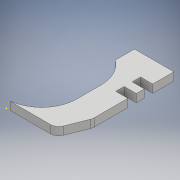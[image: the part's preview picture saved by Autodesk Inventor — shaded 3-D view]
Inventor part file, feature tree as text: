
AUTODESK INVENTOR PART (.ipt)
format: ipt  version: 2017 (Build 210142000, 142)  size: 152,064 bytes
history: native  units: mm
features: sketch x4, extrude x2, hole x1
ambient origin geometry x8: Origin, YZ Plane, XZ Plane, XY Plane, X Axis, Y Axis, Z Axis, Center Point
bodies: Solid1 (feature_tree)
feature tree (7):
  sketch  "Sketch1"  dims[d0=22.0mm d1=90.0deg]
  sketch  "Sketch2"  dims[d2=0.0mm d3=15.0mm]
  extrude  "Extrusion1"  TaperAngle=90.0deg  [1 undecoded]
  hole  "Hole1"  [1 undecoded]
  extrude  "Extrusion2"  Depth=13.0mm
  sketch  "Sketch3"  dims[d4=0.0mm d5=13.0mm]
  sketch  "Sketch4"  dims[d6=22.0mm d7=12.0mm d8=22.5mm d9=15.0mm d10=90.0mm d11=37.0mm d12=5.0mm d13=12.124057mm d14=5.2mm d15=5.2mm d16=5.0mm d17=7.5mm d18=5.0mm d19=0.0mm d20=18.0mm d21=7.5mm d22=7.5mm d23=3.5mm d24=3.4mm d25=6.0mm d26=4.0mm d27=2.0mm d28=90.0deg d29=8.0mm d30=20.594885mm d31=0.0mm d32=15.0mm d33=0.0mm]
note: 2 required parameter values undecoded (feature->parameter linkage not recoverable at this tier; creation-order binding heuristic only, values carry confidence <= 0.55)
